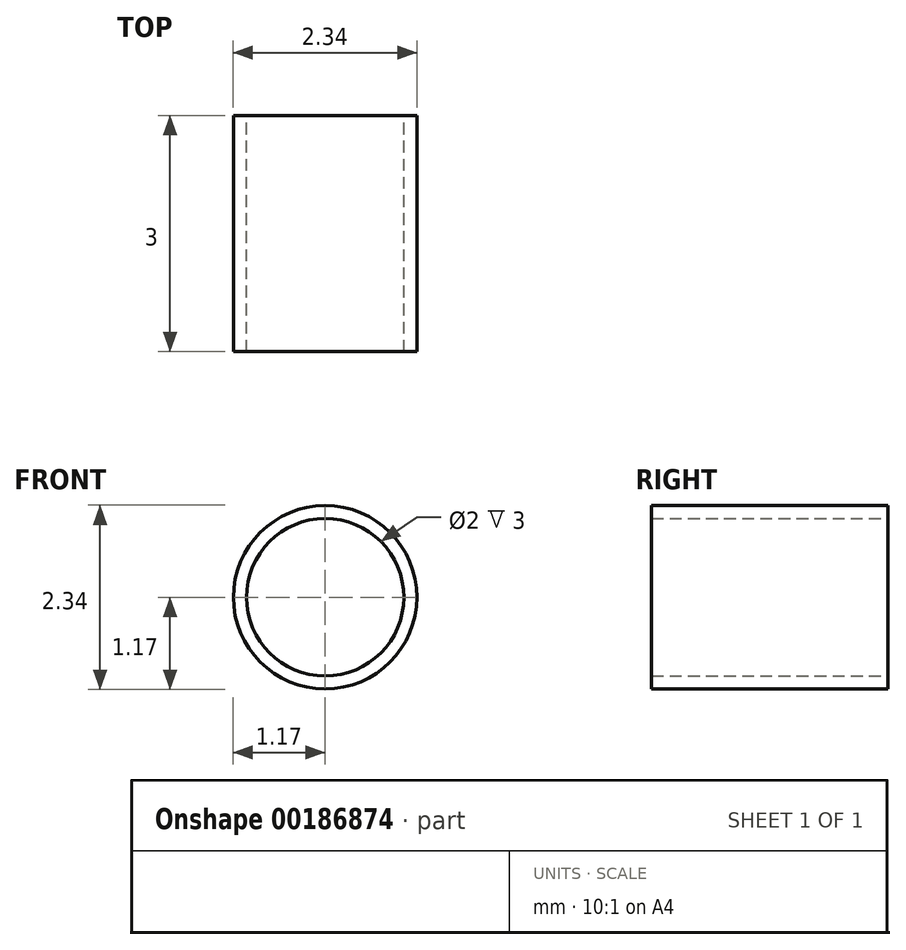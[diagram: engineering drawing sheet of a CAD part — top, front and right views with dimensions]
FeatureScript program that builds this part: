
annotation { "Feature Type Name" : "Feature", "Feature Type Description" : "" }
export const myFeature = defineFeature(function(context is Context, id is Id, definition is map)
    precondition{}
    {
        {
            var Q0;
            Q0=qCreatedBy(makeId("Front.planeOp"),FACE);
            var sketch = newSketch(context, id + "F0", { "sketchPlane" : qUnion([Q0])});
            skCircle(sketch, "E0", {"center": v(0, 0) * mm, "radius": 1 * mm});
            skCircle(sketch, "E1", {"center": v(0, 0) * mm, "radius": 1.17 * mm});
            skSolve(sketch);
        }
        {
            var Q0;
            Q0=makeQuery(id+"F0.imprint","IMPRINT",FACE,{"disambiguationData":[TD([[makeQuery(id+"F0.imprint","IMPRINT",EDGE,{"derivedFrom":sQuery(id+"F0.wireOp",EDGE,"E0")}),-1.0]])]});
            var Q1;
            Q1=makeQuery(id+"F0.imprint","IMPRINT",FACE,{"disambiguationData":[TD([[makeQuery(id+"F0.imprint","IMPRINT",EDGE,{"derivedFrom":sQuery(id+"F0.wireOp",EDGE,"E1")}),1.0]])]});
            var Q2;
            Q2=sQuery(id+"F0.wireOp",EDGE,"E1");
            extrude(context, id + "F1", {"entities" : qUnion([Q0, Q1]), "surfaceEntities" : qUnion([Q2]), "depth" : 3 * mm});
        }
    });
